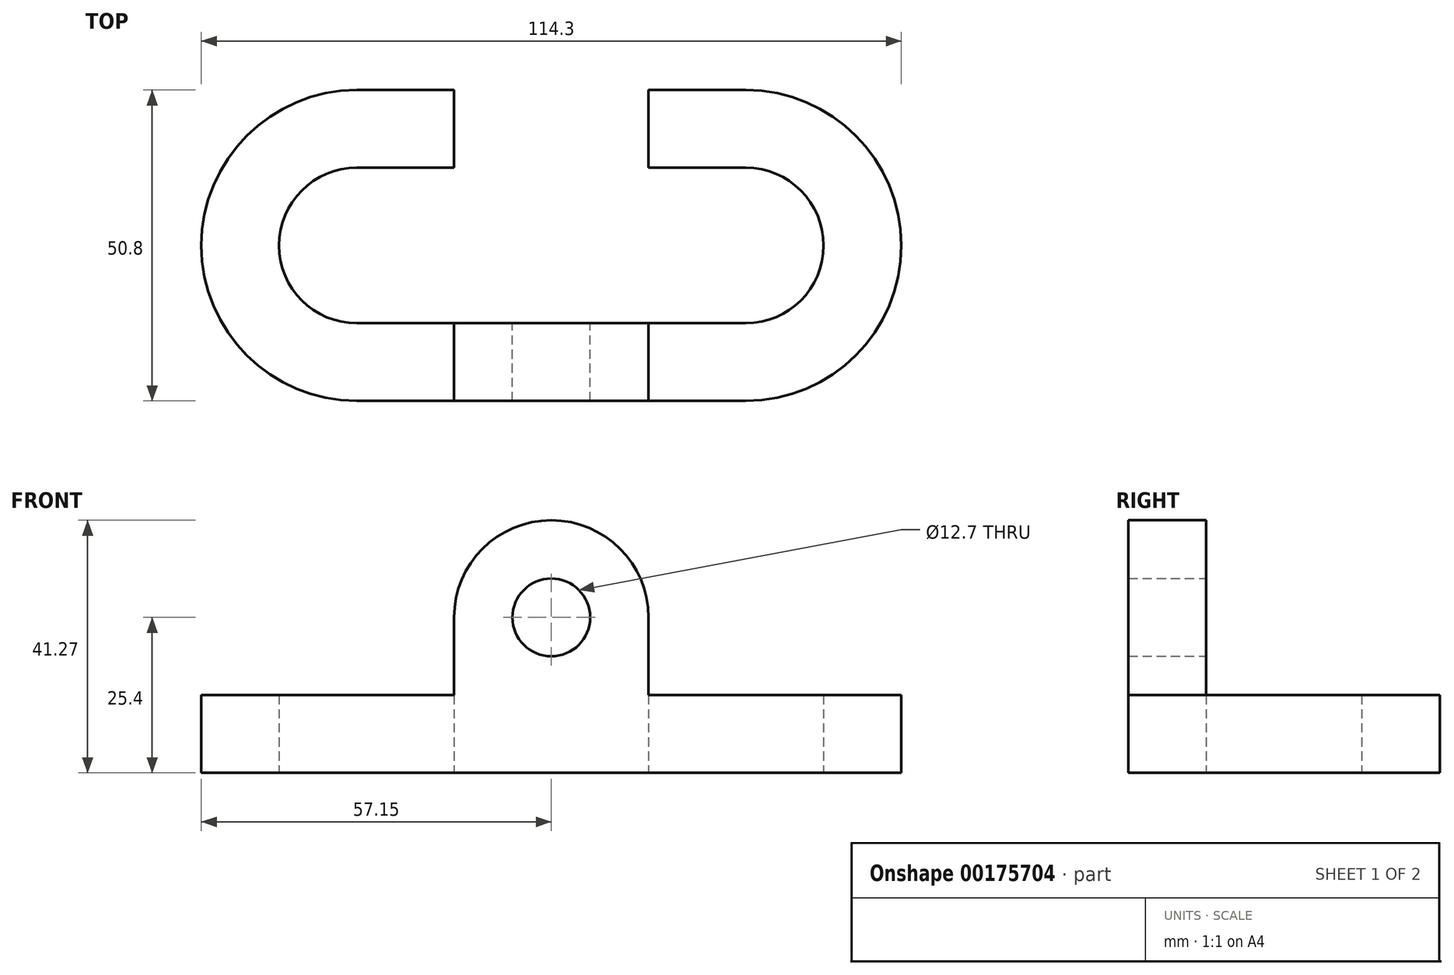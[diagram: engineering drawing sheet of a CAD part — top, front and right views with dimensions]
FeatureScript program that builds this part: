
annotation { "Feature Type Name" : "Feature", "Feature Type Description" : "" }
export const myFeature = defineFeature(function(context is Context, id is Id, definition is map)
    precondition{}
    {
        {
            var Q0;
            Q0=qCreatedBy(makeId("Front.planeOp"),FACE);
            var sketch = newSketch(context, id + "F0", { "sketchPlane" : qUnion([Q0])});
            skArc(sketch, "E0", {"start": v(0, -6.35) * mm, "mid": v(6.35, 0) * mm, "end": v(0, 6.35) * mm});
            skLineSegment(sketch, "E1", {"start": v(15.88, 0) * mm, "end": v(15.88, -25.4) * mm});
            skLineSegment(sketch, "E2", {"start": v(15.88, -25.4) * mm, "end": v(0, -25.4) * mm});
            skArc(sketch, "E3", {"start": v(15.88, 0) * mm, "mid": v(11.23, 11.23) * mm, "end": v(0, 15.88) * mm});
            skArc(sketch, "E4.MirrorCS", {"start": v(-15.88, 0) * mm, "mid": v(-11.23, 11.23) * mm, "end": v(0, 15.88) * mm});
            skLineSegment(sketch, "E5.MirrorCS", {"start": v(-15.88, 0) * mm, "end": v(-15.88, -25.4) * mm});
            skLineSegment(sketch, "E6.MirrorCS", {"start": v(-15.88, -25.4) * mm, "end": v(0, -25.4) * mm});
            skArc(sketch, "E7.MirrorCS", {"start": v(0, -6.35) * mm, "mid": v(-6.35, 0) * mm, "end": v(0, 6.35) * mm});
            skSolve(sketch);
        }
        {
            var Q0;
            Q0 = qSketchRegion(id + "F0", true);
            extrude(context, id + "F1", {"entities" : qUnion([Q0]), "depth" : 12.7 * mm});
        }
        {
            var Q0;
            Q0=makeQuery(id+"F1.opExtrude","SWEPT_FACE",FACE,{"disambiguationData":[OSD([sQuery(id+"F0.wireOp",EDGE,"E2"),sQuery(id+"F0.wireOp",EDGE,"E6.MirrorCS")])]});
            var sketch = newSketch(context, id + "F2", { "sketchPlane" : qUnion([Q0])});
            skLineSegment(sketch, "E8.bottom", {"start": v(15.88, 0) * mm, "end": v(31.75, 0) * mm});
            skLineSegment(sketch, "E8.top", {"start": v(15.88, 12.7) * mm, "end": v(31.75, 12.7) * mm});
            skLineSegment(sketch, "E8.left", {"start": v(15.88, 0) * mm, "end": v(15.88, 12.7) * mm});
            skLineSegment(sketch, "E8.right", {"start": v(31.75, 0) * mm, "end": v(31.75, 12.7) * mm});
            skLineSegment(sketch, "E9.bottom", {"start": v(15.88, -25.4) * mm, "end": v(31.75, -25.4) * mm});
            skLineSegment(sketch, "E9.top", {"start": v(15.88, -38.1) * mm, "end": v(31.75, -38.1) * mm});
            skLineSegment(sketch, "E9.left", {"start": v(15.88, -25.4) * mm, "end": v(15.88, -38.1) * mm});
            skLineSegment(sketch, "E9.right", {"start": v(31.75, -25.4) * mm, "end": v(31.75, -38.1) * mm});
            skArc(sketch, "E10", {"start": v(31.75, -38.1) * mm, "mid": v(57.15, -12.7) * mm, "end": v(31.75, 12.7) * mm});
            skArc(sketch, "E11", {"start": v(31.75, -25.4) * mm, "mid": v(44.45, -12.7) * mm, "end": v(31.75, 0) * mm});
            skLineSegment(sketch, "E12", {"start": v(0, 35.69) * mm, "end": v(0, -57.47) * mm});
            skLineSegment(sketch, "E13.MirrorCS", {"start": v(-15.88, 12.7) * mm, "end": v(-31.75, 12.7) * mm});
            skLineSegment(sketch, "E14.MirrorCS", {"start": v(-31.75, 0) * mm, "end": v(-31.75, 12.7) * mm});
            skLineSegment(sketch, "E15.MirrorCS", {"start": v(-15.88, 0) * mm, "end": v(-15.88, 12.7) * mm});
            skLineSegment(sketch, "E16.MirrorCS", {"start": v(-15.88, 0) * mm, "end": v(-31.75, 0) * mm});
            skArc(sketch, "E17.MirrorCS", {"start": v(-31.75, -38.1) * mm, "mid": v(-57.15, -12.7) * mm, "end": v(-31.75, 12.7) * mm});
            skArc(sketch, "E18.MirrorCS", {"start": v(-31.75, -25.4) * mm, "mid": v(-44.45, -12.7) * mm, "end": v(-31.75, 0) * mm});
            skLineSegment(sketch, "E19.MirrorCS", {"start": v(-31.75, -25.4) * mm, "end": v(-31.75, -38.1) * mm});
            skLineSegment(sketch, "E20.MirrorCS", {"start": v(-15.88, -25.4) * mm, "end": v(-31.75, -25.4) * mm});
            skLineSegment(sketch, "E21.MirrorCS", {"start": v(-15.88, -38.1) * mm, "end": v(-31.75, -38.1) * mm});
            skLineSegment(sketch, "E22.MirrorCS", {"start": v(-15.88, -25.4) * mm, "end": v(-15.88, -38.1) * mm});
            skSolve(sketch);
        }
        {
            var Q0;
            Q0=makeQuery(id+"F2.imprint","IMPRINT",FACE,{"disambiguationData":[TD([[makeQuery(id+"F2.imprint","IMPRINT",EDGE,{"derivedFrom":sQuery(id+"F2.wireOp",EDGE,"E14.MirrorCS")}),1.0]])]});
            var Q1;
            Q1=makeQuery(id+"F2.imprint","IMPRINT",FACE,{"disambiguationData":[TD([[makeQuery(id+"F2.imprint","IMPRINT",EDGE,{"derivedFrom":sQuery(id+"F2.wireOp",EDGE,"E13.MirrorCS")}),1.0]])]});
            var Q2;
            Q2=makeQuery(id+"F2.imprint","IMPRINT",FACE,{"disambiguationData":[TD([[makeQuery(id+"F2.imprint","IMPRINT",EDGE,{"derivedFrom":sQuery(id+"F2.wireOp",EDGE,"E19.MirrorCS")}),1.0]])]});
            var Q3;
            Q3=makeQuery(id+"F2.imprint","IMPRINT",FACE,{"disambiguationData":[TD([[makeQuery(id+"F2.imprint","IMPRINT",EDGE,{"derivedFrom":sQuery(id+"F2.wireOp",EDGE,"E8.bottom")}),1.0]])]});
            var Q4;
            Q4=makeQuery(id+"F2.imprint","IMPRINT",FACE,{"disambiguationData":[TD([[makeQuery(id+"F2.imprint","IMPRINT",EDGE,{"derivedFrom":sQuery(id+"F2.wireOp",EDGE,"E8.right")}),-1.0]])]});
            var Q5;
            Q5=makeQuery(id+"F2.imprint","IMPRINT",FACE,{"disambiguationData":[TD([[makeQuery(id+"F2.imprint","IMPRINT",EDGE,{"derivedFrom":sQuery(id+"F2.wireOp",EDGE,"E9.bottom")}),-1.0]])]});
            extrude(context, id + "F3", {"entities" : qUnion([Q0, Q1, Q2, Q3, Q4, Q5]), "operationType" : NewBodyOperationType.ADD, "oppositeDirection" : true, "depth" : 12.7 * mm});
        }
    });
